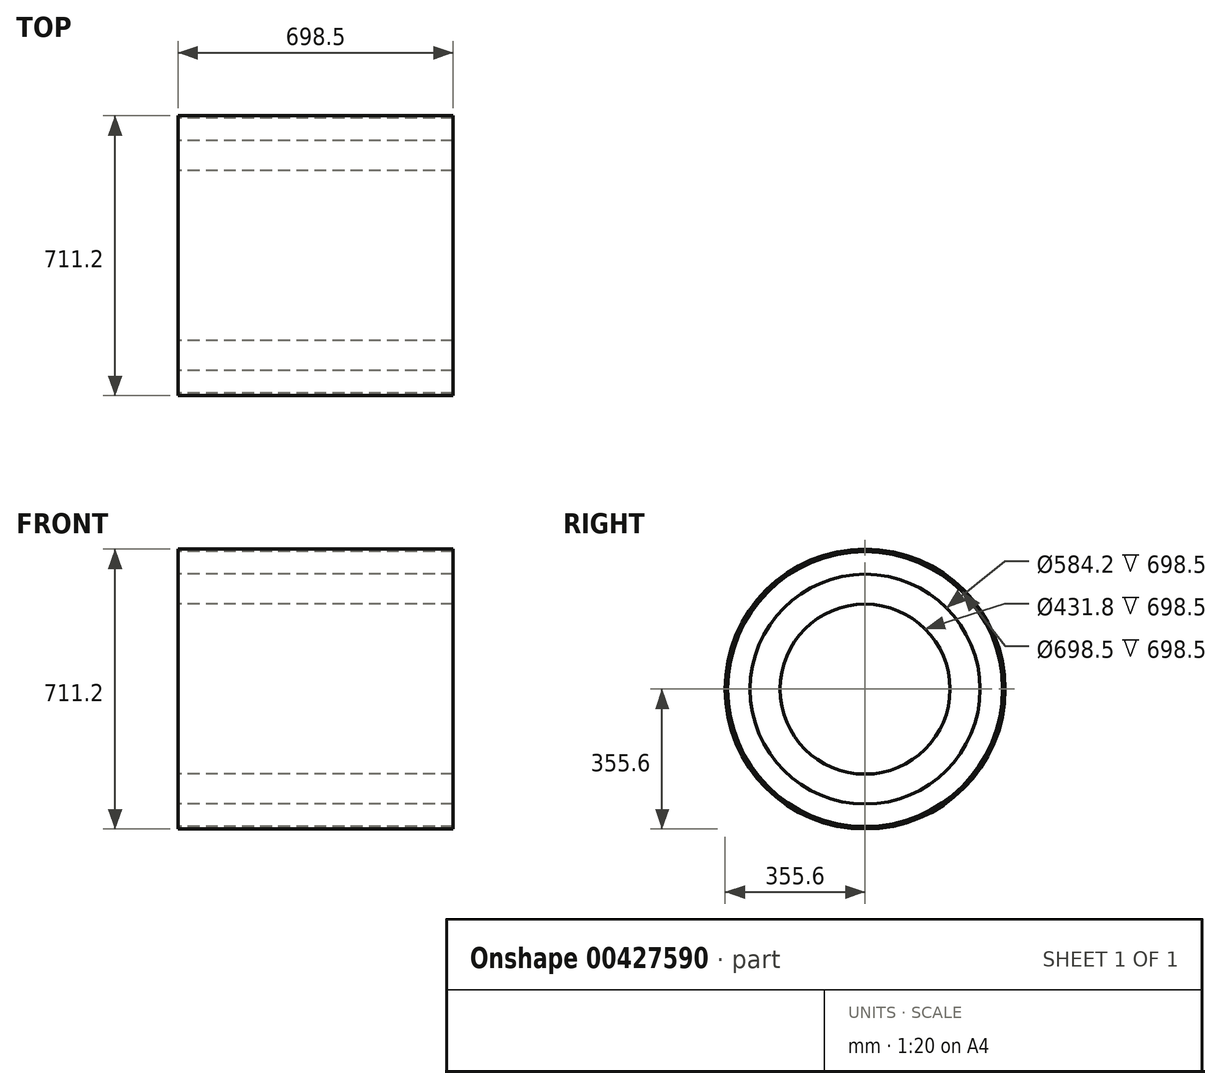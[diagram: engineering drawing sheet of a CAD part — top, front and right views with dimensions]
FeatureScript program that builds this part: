
annotation { "Feature Type Name" : "Feature", "Feature Type Description" : "" }
export const myFeature = defineFeature(function(context is Context, id is Id, definition is map)
    precondition{}
    {
        {
            var Q0;
            Q0=qCreatedBy(makeId("Front.planeOp"),FACE);
            var sketch = newSketch(context, id + "F0", { "sketchPlane" : qUnion([Q0])});
            skLineSegment(sketch, "E0", {"start": v(-134, 0) * mm, "end": v(144.6, 0) * mm, "construction": true});
            skLineSegment(sketch, "E1", {"start": v(0, 0) * mm, "end": v(0, 215.9) * mm});
            skLineSegment(sketch, "E2", {"start": v(0, 215.9) * mm, "end": v(0, 292.1) * mm});
            skPoint(sketch, "E2.endSnap0", {"position": v(0, 107.95) * mm});
            skLineSegment(sketch, "E3", {"start": v(0, 292.1) * mm, "end": v(0, 349.25) * mm});
            skLineSegment(sketch, "E4", {"start": v(0, 349.25) * mm, "end": v(0, 355.6) * mm});
            skLineSegment(sketch, "E5", {"start": v(0, 355.6) * mm, "end": v(-698.5, 355.6) * mm});
            skLineSegment(sketch, "E6", {"start": v(-698.5, 355.6) * mm, "end": v(-698.5, 349.25) * mm});
            skLineSegment(sketch, "E7", {"start": v(-698.5, 349.25) * mm, "end": v(-698.5, 292.1) * mm});
            skLineSegment(sketch, "E8", {"start": v(-698.5, 292.1) * mm, "end": v(-698.5, 215.9) * mm});
            skLineSegment(sketch, "E9", {"start": v(-698.5, 215.9) * mm, "end": v(0, 215.9) * mm});
            skLineSegment(sketch, "E10", {"start": v(0, 292.1) * mm, "end": v(-698.5, 292.1) * mm});
            skLineSegment(sketch, "E11", {"start": v(-698.5, 349.25) * mm, "end": v(0, 349.25) * mm});
            skSolve(sketch);
        }
        {
            var Q0;
            Q0=makeQuery(id+"F0.imprint","IMPRINT",FACE,{"disambiguationData":[TD([[makeQuery(id+"F0.imprint","IMPRINT",EDGE,{"derivedFrom":sQuery(id+"F0.wireOp",EDGE,"E4")}),1.0]])]});
            var Q1;
            Q1=sQuery(id+"F0.wireOp",EDGE,"E0");
            revolve(context, id + "F1", {"entities" : qUnion([Q0]), "axis" : qUnion([Q1]), "revolveType" : RevolveType.FULL});
        }
        {
            var Q0;
            Q0=makeQuery(id+"F0.imprint","IMPRINT",FACE,{"disambiguationData":[TD([[makeQuery(id+"F0.imprint","IMPRINT",EDGE,{"derivedFrom":sQuery(id+"F0.wireOp",EDGE,"E3")}),1.0]])]});
            var Q1;
            Q1=sQuery(id+"F0.wireOp",EDGE,"E0");
            revolve(context, id + "F2", {"entities" : qUnion([Q0]), "axis" : qUnion([Q1]), "revolveType" : RevolveType.FULL});
        }
        {
            var Q0;
            Q0=makeQuery(id+"F0.imprint","IMPRINT",FACE,{"disambiguationData":[TD([[makeQuery(id+"F0.imprint","IMPRINT",EDGE,{"derivedFrom":sQuery(id+"F0.wireOp",EDGE,"E2")}),1.0]])]});
            var Q1;
            Q1=sQuery(id+"F0.wireOp",EDGE,"E0");
            revolve(context, id + "F3", {"entities" : qUnion([Q0]), "axis" : qUnion([Q1]), "revolveType" : RevolveType.FULL});
        }
    });
